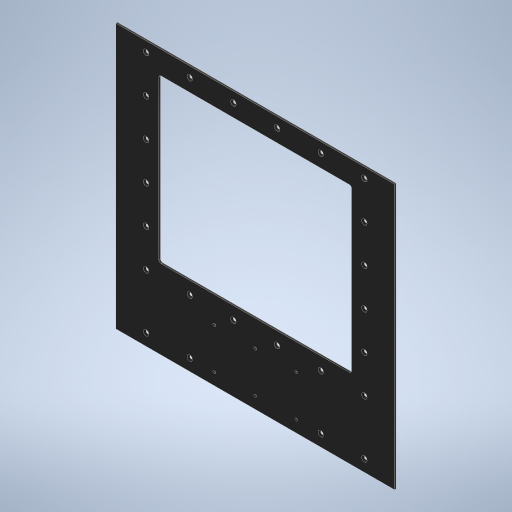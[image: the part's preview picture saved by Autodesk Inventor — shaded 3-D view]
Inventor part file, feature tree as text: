
AUTODESK INVENTOR PART (.ipt)
format: ipt  version: 2024 (Build 280153000, 153)  size: 324,608 bytes
history: native  units: mm
features: sketch x4, extrude x2, hole x2, fillet x1
ambient origin geometry x8: Origin, YZ Plane, XZ Plane, XY Plane, X Axis, Y Axis, Z Axis, Center Point
bodies: Solid1 (feature_tree)
feature tree (9):
  extrude  "Extrusion1"  Depth=485.0mm
  sketch  "Sketch4"  dims[d19=100.0mm d21=445.0mm d29=400.0mm]
  hole  "Hole1"  [1 undecoded]
  sketch  "Sketch Driven Pattern1"  dims[d0=511.0mm d1=485.0mm]
  extrude  "Extrusion4"  Depth=445.0mm
  fillet  "Fillet2"  Radius=400.0mm
  hole  "Hole2"  [1 undecoded]
  sketch  "Sketch1"  dims[d2=3.0mm d3=0.0mm d18=21.35mm]
  sketch  "Sketch5"  dims[d30=12.0mm d31=12.0mm d39=40.0mm d41=69.0mm d42=10.0mm d44=10.0mm d47=12.0mm d48=5.4mm d49=10.0mm d50=10.4mm d51=2.0mm d52=90.0deg d53=8.0mm d54=20.594885mm d55=69.0mm d56=0.0mm d57=0.0mm d58=11.5mm d59=4.0mm d61=5.3mm d62=6.0mm d63=10.4mm d64=2.0mm d65=90.0deg d66=8.0mm d67=20.594885mm d68=60.0mm d70=80.0mm d71=10.0mm d73=10.0mm d75=60.0mm d77=80.0mm d78=10.0mm d80=10.0mm d82=60.0mm d84=80.0mm d85=10.0mm d87=10.0mm d89=150.0mm d90=75.0mm d69=1.0mm d72=5.4mm d74=14.3117mm d76=20.594885mm d79=0.375mm]
note: 2 required parameter values undecoded (feature->parameter linkage not recoverable at this tier; creation-order binding heuristic only, values carry confidence <= 0.55)
